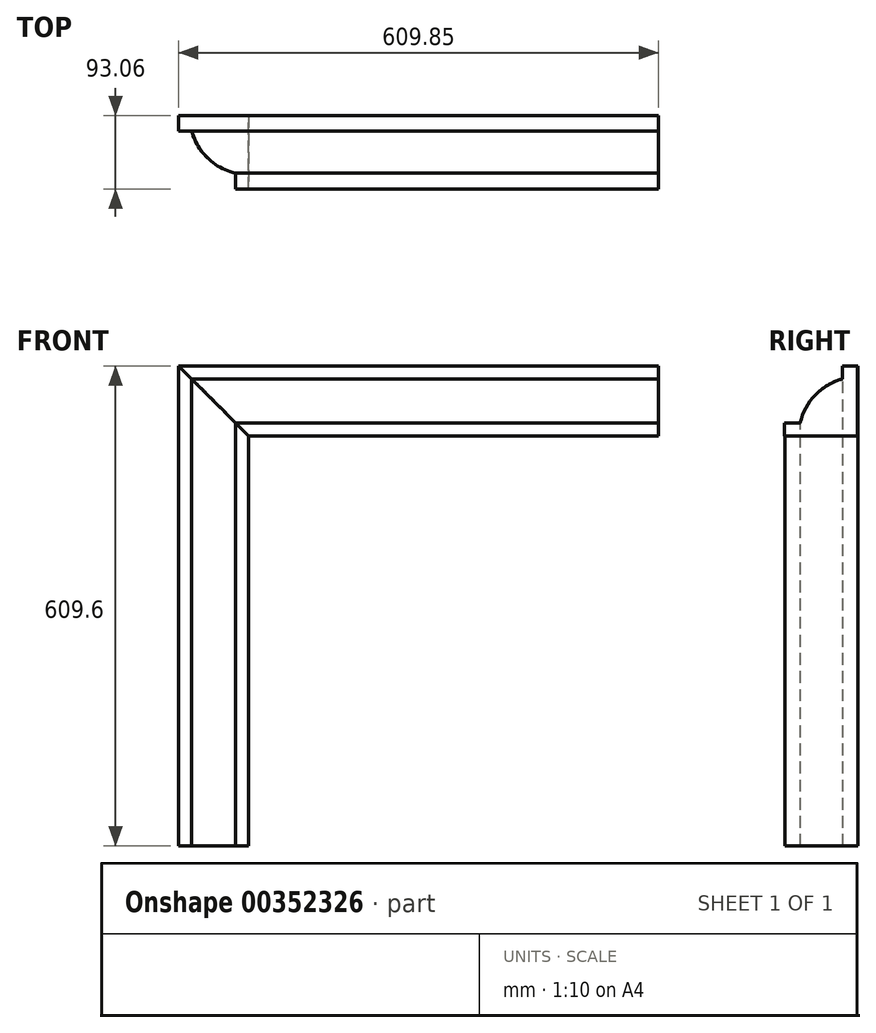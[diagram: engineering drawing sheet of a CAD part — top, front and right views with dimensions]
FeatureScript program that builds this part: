
annotation { "Feature Type Name" : "Feature", "Feature Type Description" : "" }
export const myFeature = defineFeature(function(context is Context, id is Id, definition is map)
    precondition{}
    {
        {
            var Q0;
            Q0=qCreatedBy(makeId("Right.planeOp"),FACE);
            var sketch = newSketch(context, id + "F0", { "sketchPlane" : qUnion([Q0])});
            skArc(sketch, "E0", {"start": v(-19.16, 72.3) * mm, "mid": v(-53.85, 51.9) * mm, "end": v(-72.95, 16.5) * mm});
            skLineSegment(sketch, "E1", {"start": v(-19.16, 72.3) * mm, "end": v(-19.16, 88.9) * mm});
            skLineSegment(sketch, "E2", {"start": v(-19.16, 88.9) * mm, "end": v(0, 88.9) * mm});
            skLineSegment(sketch, "E3", {"start": v(0, 88.9) * mm, "end": v(0, 0) * mm});
            skLineSegment(sketch, "E4", {"start": v(-92.82, 0) * mm, "end": v(-92.82, 16.52) * mm});
            skLineSegment(sketch, "E5", {"start": v(-92.82, 16.52) * mm, "end": v(-72.95, 16.5) * mm});
            skLineSegment(sketch, "E6", {"start": v(0, 0) * mm, "end": v(-92.82, 0) * mm});
            skSolve(sketch);
        }
        {
            var Q0;
            Q0=makeQuery(id+"F0.imprint","IMPRINT",FACE,{"disambiguationData":[TD([[makeQuery(id+"F0.imprint","IMPRINT",EDGE,{"derivedFrom":sQuery(id+"F0.wireOp",EDGE,"E0")}),1.0]])]});
            extrude(context, id + "F1", {"entities" : qUnion([Q0]), "depth" : 609.6 * mm});
        }
        {
            var Q0;
            Q0=qCreatedBy(makeId("Front.planeOp"),FACE);
            var sketch = newSketch(context, id + "F2", { "sketchPlane" : qUnion([Q0])});
            skLineSegment(sketch, "E7", {"start": v(0, 88.9) * mm, "end": v(88.9, 0) * mm});
            skLineSegment(sketch, "E8", {"start": v(88.9, 0) * mm, "end": v(0, 0) * mm});
            skLineSegment(sketch, "E9", {"start": v(0, 0) * mm, "end": v(0, 88.9) * mm});
            skSolve(sketch);
        }
        {
            var Q0;
            Q0=makeQuery(id+"F2.imprint","IMPRINT",FACE,{"disambiguationData":[TD([[makeQuery(id+"F2.imprint","IMPRINT",EDGE,{"derivedFrom":sQuery(id+"F2.wireOp",EDGE,"E7")}),-1.0]])]});
            extrude(context, id + "F3", {"entities" : qUnion([Q0]), "operationType" : NewBodyOperationType.REMOVE, "endBound" : BoundingType.THROUGH_ALL, "depth" : 25.4 * mm});
        }
        {
            var Q0;
            Q0=qCreatedBy(makeId("Top.planeOp"),FACE);
            cPlane(context, id + "F4", {"entities" : qUnion([Q0]), "cplaneType" : CPlaneType.OFFSET, "offset" : 88.9 * mm, "width" : 152.4 * mm, "height" : 152.4 * mm});
        }
        {
            var Q0;
            Q0=qCreatedBy(id+"F4.planeOp",FACE);
            var sketch = newSketch(context, id + "F5", { "sketchPlane" : qUnion([Q0])});
            skArc(sketch, "E10", {"start": v(16.36, -18.92) * mm, "mid": v(36.75, -53.6) * mm, "end": v(72.16, -72.71) * mm});
            skLineSegment(sketch, "E11", {"start": v(16.36, -18.92) * mm, "end": v(-0.25, -18.92) * mm});
            skLineSegment(sketch, "E12", {"start": v(-0.25, -18.92) * mm, "end": v(-0.25, 0.24) * mm});
            skLineSegment(sketch, "E13", {"start": v(-0.25, 0.24) * mm, "end": v(88.65, 0.24) * mm});
            skLineSegment(sketch, "E14", {"start": v(88.65, -92.58) * mm, "end": v(72.14, -92.58) * mm});
            skLineSegment(sketch, "E15", {"start": v(72.14, -92.58) * mm, "end": v(72.16, -72.71) * mm});
            skLineSegment(sketch, "E16", {"start": v(88.65, 0.24) * mm, "end": v(88.65, -92.58) * mm});
            skPoint(sketch, "E17", {"position": v(48.4, -62.8) * mm});
            skSolve(sketch);
        }
        {
            var Q0;
            Q0=makeQuery(id+"F5.imprint","IMPRINT",FACE,{"disambiguationData":[TD([[makeQuery(id+"F5.imprint","IMPRINT",EDGE,{"derivedFrom":sQuery(id+"F5.wireOp",EDGE,"E10")}),1.0]])]});
            extrude(context, id + "F6", {"entities" : qUnion([Q0]), "oppositeDirection" : true, "depth" : 609.6 * mm});
        }
        {
            var Q0;
            Q0=makeQuery(id+"F1.opExtrude","SWEPT_BODY",BODY,{"disambiguationData":[OSD([sQuery(id+"F0.wireOp",EDGE,"E0"),sQuery(id+"F0.wireOp",EDGE,"E1"),sQuery(id+"F0.wireOp",EDGE,"E2"),sQuery(id+"F0.wireOp",EDGE,"E3"),sQuery(id+"F0.wireOp",EDGE,"E4"),sQuery(id+"F0.wireOp",EDGE,"E5"),sQuery(id+"F0.wireOp",EDGE,"E6")])]});
            transform(context, id + "F7", {"entities" : qUnion([Q0]), "transformType" : TransformType.TRANSLATION_3D, "dx" : 175.26 * mm, "dy" : 0 * mm, "dz" : 0 * mm, "makeCopy" : false});
        }
        {
            var Q0;
            Q0=qCreatedBy(makeId("Front.planeOp"),FACE);
            var sketch = newSketch(context, id + "F8", { "sketchPlane" : qUnion([Q0])});
            skLineSegment(sketch, "E18", {"start": v(0, 88.9) * mm, "end": v(88.9, 0) * mm});
            skLineSegment(sketch, "E19", {"start": v(88.9, 0) * mm, "end": v(88.9, 88.9) * mm});
            skLineSegment(sketch, "E20", {"start": v(88.9, 88.9) * mm, "end": v(0, 88.9) * mm});
            skSolve(sketch);
        }
        {
            var Q0;
            Q0=makeQuery(id+"F8.imprint","IMPRINT",FACE,{"disambiguationData":[TD([[makeQuery(id+"F8.imprint","IMPRINT",EDGE,{"derivedFrom":sQuery(id+"F8.wireOp",EDGE,"E18")}),1.0]])]});
            extrude(context, id + "F9", {"entities" : qUnion([Q0]), "operationType" : NewBodyOperationType.REMOVE, "endBound" : BoundingType.SYMMETRIC, "depth" : 203.2 * mm});
        }
        {
            var Q0;
            Q0=makeQuery(id+"F1.opExtrude","SWEPT_BODY",BODY,{"disambiguationData":[OSD([sQuery(id+"F0.wireOp",EDGE,"E0"),sQuery(id+"F0.wireOp",EDGE,"E1"),sQuery(id+"F0.wireOp",EDGE,"E2"),sQuery(id+"F0.wireOp",EDGE,"E3"),sQuery(id+"F0.wireOp",EDGE,"E4"),sQuery(id+"F0.wireOp",EDGE,"E5"),sQuery(id+"F0.wireOp",EDGE,"E6")])]});
            transform(context, id + "F10", {"entities" : qUnion([Q0]), "transformType" : TransformType.TRANSLATION_3D, "dx" : -175.26 * mm, "dy" : 0 * mm, "dz" : 0 * mm, "makeCopy" : false});
        }
    });
